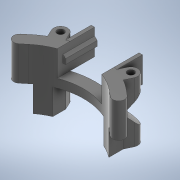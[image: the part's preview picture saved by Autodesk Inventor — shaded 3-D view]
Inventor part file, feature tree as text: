
AUTODESK INVENTOR PART (.ipt)
format: ipt  version: 2020 (Build 240168000, 168)  size: 553,472 bytes
history: native  units: mm
features: sketch x8, extrude x7, projected_geometry x5, other x2, sweep x1
ambient origin geometry x8: Origin, YZ Plane, XZ Plane, XY Plane, X Axis, Y Axis, Z Axis, Center Point
bodies: Body1 (feature_tree)
feature tree (23):
  other  "Твердое тело1"
  extrude  "Выдавливание1"  Depth=35.0mm TaperAngle=0.0deg
  sketch  "Эскиз2"
  extrude  "Выдавливание2"  Depth=4.0mm
  sweep  "Сдвиг1"
  extrude  "Выдавливание5"  Depth=8.0mm
  extrude  "Выдавливание6"  Depth=35.0mm TaperAngle=0.0deg
  extrude  "Выдавливание7"  Depth=8.5mm
  extrude  "Выдавливание8"  TaperAngle=45.0deg  [1 undecoded]
  other  "РабПлоскость1"
  extrude  "Выдавливание9"  Depth=8.5mm
  sketch  "Эскиз1"
  sketch  "Эскиз3"
  projected_geometry  "Спроецированная петля1"
  projected_geometry  "Спроецированная петля2"
  sketch  "3D эскиз1"
  sketch  "Эскиз4"
  sketch  "Эскиз6"
  projected_geometry  "Спроецированная петля4"
  sketch  "Эскиз7"
  projected_geometry  "Спроецированная петля5"
  sketch  "Эскиз9"
  projected_geometry  "Спроецированная петля7"
note: 1 required parameter value undecoded (feature->parameter linkage not recoverable at this tier; creation-order binding heuristic only, values carry confidence <= 0.55)
